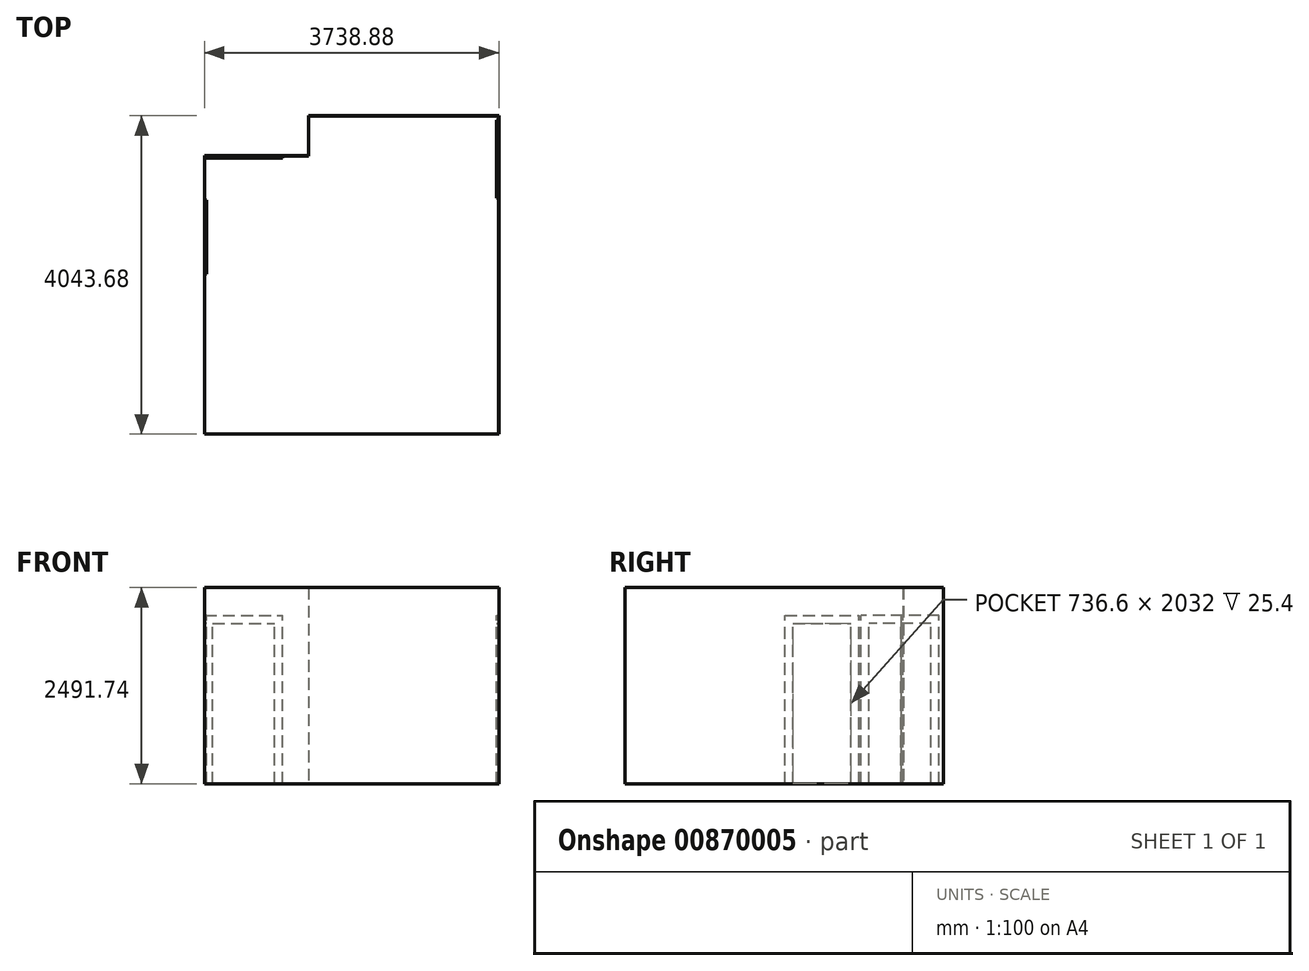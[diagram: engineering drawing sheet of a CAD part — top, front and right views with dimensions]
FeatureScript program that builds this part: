
annotation { "Feature Type Name" : "Feature", "Feature Type Description" : "" }
export const myFeature = defineFeature(function(context is Context, id is Id, definition is map)
    precondition{}
    {
        {
            var Q0;
            Q0=qCreatedBy(makeId("Top.planeOp"),FACE);
            var sketch = newSketch(context, id + "F0", { "sketchPlane" : qUnion([Q0])});
            skLineSegment(sketch, "E0.bottom", {"start": v(0, 0) * mm, "end": v(3733.8, 0) * mm});
            skLineSegment(sketch, "E0.top", {"start": v(1320.8, 4038.6) * mm, "end": v(3733.8, 4038.6) * mm});
            skLineSegment(sketch, "E0.left", {"start": v(0, 0) * mm, "end": v(0, 3530.6) * mm});
            skLineSegment(sketch, "E0.right", {"start": v(3733.8, 0) * mm, "end": v(3733.8, 4038.6) * mm});
            skLineSegment(sketch, "E1.top", {"start": v(0, 3530.6) * mm, "end": v(1320.8, 3530.6) * mm});
            skLineSegment(sketch, "E1.right", {"start": v(1320.8, 4038.6) * mm, "end": v(1320.8, 3530.6) * mm});
            skSolve(sketch);
        }
        {
            var Q0;
            Q0=makeQuery(id+"F0.imprint","IMPRINT",FACE,{"disambiguationData":[TD([[makeQuery(id+"F0.imprint","IMPRINT",EDGE,{"derivedFrom":sQuery(id+"F0.wireOp",EDGE,"E0.bottom")}),1.0]])]});
            extrude(context, id + "F1", {"entities" : qUnion([Q0]), "depth" : 2489.2 * mm, "offsetDistance" : 25.4 * mm});
        }
        {
            var Q0;
            Q0=makeQuery(id+"F1.opExtrude","CAP_FACE",FACE,{"disambiguationData":[OSD([sQuery(id+"F0.wireOp",EDGE,"E0.bottom"),sQuery(id+"F0.wireOp",EDGE,"E0.top"),sQuery(id+"F0.wireOp",EDGE,"E0.left"),sQuery(id+"F0.wireOp",EDGE,"E0.right"),sQuery(id+"F0.wireOp",EDGE,"E1.top"),sQuery(id+"F0.wireOp",EDGE,"E1.right")])],"isStart":false});
            shell(context, id + "F2", {"entities" : qUnion([Q0]), "thickness" : 2.54 * mm, "oppositeDirection" : true});
        }
        {
            var Q0;
            Q0=makeQuery(id+"F2.opShell","OFFSET_FACE",FACE,{"disambiguationData":[OSD([sQuery(id+"F0.wireOp",EDGE,"E0.right")])]});
            var sketch = newSketch(context, id + "F3", { "sketchPlane" : qUnion([Q0])});
            skLineSegment(sketch, "E2.bottom", {"start": v(-3987.8, 0) * mm, "end": v(-2997.2, 0) * mm});
            skLineSegment(sketch, "E2.top", {"start": v(-3987.8, 2133.6) * mm, "end": v(-2997.2, 2133.6) * mm});
            skLineSegment(sketch, "E2.left", {"start": v(-3987.8, 0) * mm, "end": v(-3987.8, 2133.6) * mm});
            skLineSegment(sketch, "E2.right", {"start": v(-2997.2, 0) * mm, "end": v(-2997.2, 2133.6) * mm});
            skLineSegment(sketch, "E3.bottom", {"start": v(-3886.2, 0) * mm, "end": v(-3098.8, 0) * mm});
            skLineSegment(sketch, "E3.top", {"start": v(-3886.2, 2032) * mm, "end": v(-3098.8, 2032) * mm});
            skLineSegment(sketch, "E3.left", {"start": v(-3886.2, 0) * mm, "end": v(-3886.2, 2032) * mm});
            skLineSegment(sketch, "E3.right", {"start": v(-3098.8, 0) * mm, "end": v(-3098.8, 2032) * mm});
            skSolve(sketch);
        }
        {
            var Q0;
            Q0=makeQuery(id+"F3.imprint","IMPRINT",FACE,{"disambiguationData":[TD([[makeQuery(id+"F3.imprint","IMPRINT",EDGE,{"derivedFrom":sQuery(id+"F3.wireOp",EDGE,"E2.bottom")}),-1.0]])]});
            extrude(context, id + "F4", {"entities" : qUnion([Q0]), "operationType" : NewBodyOperationType.ADD, "depth" : 25.4 * mm, "offsetDistance" : 25.4 * mm});
        }
        {
            var Q0;
            Q0=makeQuery(id+"F2.opShell","OFFSET_FACE",FACE,{"disambiguationData":[OSD([sQuery(id+"F0.wireOp",EDGE,"E1.top")])]});
            var sketch = newSketch(context, id + "F5", { "sketchPlane" : qUnion([Q0])});
            skLineSegment(sketch, "E4.bottom", {"start": v(0, 0) * mm, "end": v(990.6, 0) * mm});
            skLineSegment(sketch, "E4.top", {"start": v(0, 2133.6) * mm, "end": v(990.6, 2133.6) * mm});
            skLineSegment(sketch, "E4.left", {"start": v(0, 0) * mm, "end": v(0, 2133.6) * mm});
            skLineSegment(sketch, "E4.right", {"start": v(990.6, 0) * mm, "end": v(990.6, 2133.6) * mm});
            skLineSegment(sketch, "E5.bottom", {"start": v(101.6, 0) * mm, "end": v(889, 0) * mm});
            skLineSegment(sketch, "E5.top", {"start": v(101.6, 2032) * mm, "end": v(889, 2032) * mm});
            skLineSegment(sketch, "E5.left", {"start": v(101.6, 0) * mm, "end": v(101.6, 2032) * mm});
            skLineSegment(sketch, "E5.right", {"start": v(889, 0) * mm, "end": v(889, 2032) * mm});
            skSolve(sketch);
        }
        {
            var Q0;
            Q0=makeQuery(id+"F5.imprint","IMPRINT",FACE,{"disambiguationData":[TD([[makeQuery(id+"F5.imprint","IMPRINT",EDGE,{"derivedFrom":sQuery(id+"F5.wireOp",EDGE,"E4.top")}),-1.0]])]});
            extrude(context, id + "F6", {"entities" : qUnion([Q0]), "operationType" : NewBodyOperationType.ADD, "depth" : 25.4 * mm, "offsetDistance" : 25.4 * mm});
        }
        {
            var Q0;
            Q0=makeQuery(id+"F2.opShell","OFFSET_FACE",FACE,{"disambiguationData":[OSD([sQuery(id+"F0.wireOp",EDGE,"E0.left")])]});
            var sketch = newSketch(context, id + "F7", { "sketchPlane" : qUnion([Q0])});
            skLineSegment(sketch, "E6.bottom", {"start": v(2032, 0) * mm, "end": v(2971.8, 0) * mm});
            skLineSegment(sketch, "E6.top", {"start": v(2032, 2133.6) * mm, "end": v(2971.8, 2133.6) * mm});
            skLineSegment(sketch, "E6.left", {"start": v(2032, 0) * mm, "end": v(2032, 2133.6) * mm});
            skLineSegment(sketch, "E6.right", {"start": v(2971.8, 0) * mm, "end": v(2971.8, 2133.6) * mm});
            skLineSegment(sketch, "E7.bottom", {"start": v(2133.6, 0) * mm, "end": v(2870.2, 0) * mm});
            skLineSegment(sketch, "E7.top", {"start": v(2133.6, 2032) * mm, "end": v(2870.2, 2032) * mm});
            skLineSegment(sketch, "E7.left", {"start": v(2133.6, 0) * mm, "end": v(2133.6, 2032) * mm});
            skLineSegment(sketch, "E7.right", {"start": v(2870.2, 0) * mm, "end": v(2870.2, 2032) * mm});
            skSolve(sketch);
        }
        {
            var Q0;
            Q0=makeQuery(id+"F7.imprint","IMPRINT",FACE,{"disambiguationData":[TD([[makeQuery(id+"F7.imprint","IMPRINT",EDGE,{"derivedFrom":sQuery(id+"F7.wireOp",EDGE,"E6.top")}),-1.0]])]});
            extrude(context, id + "F8", {"entities" : qUnion([Q0]), "operationType" : NewBodyOperationType.ADD, "depth" : 25.4 * mm, "offsetDistance" : 25.4 * mm});
        }
    });
